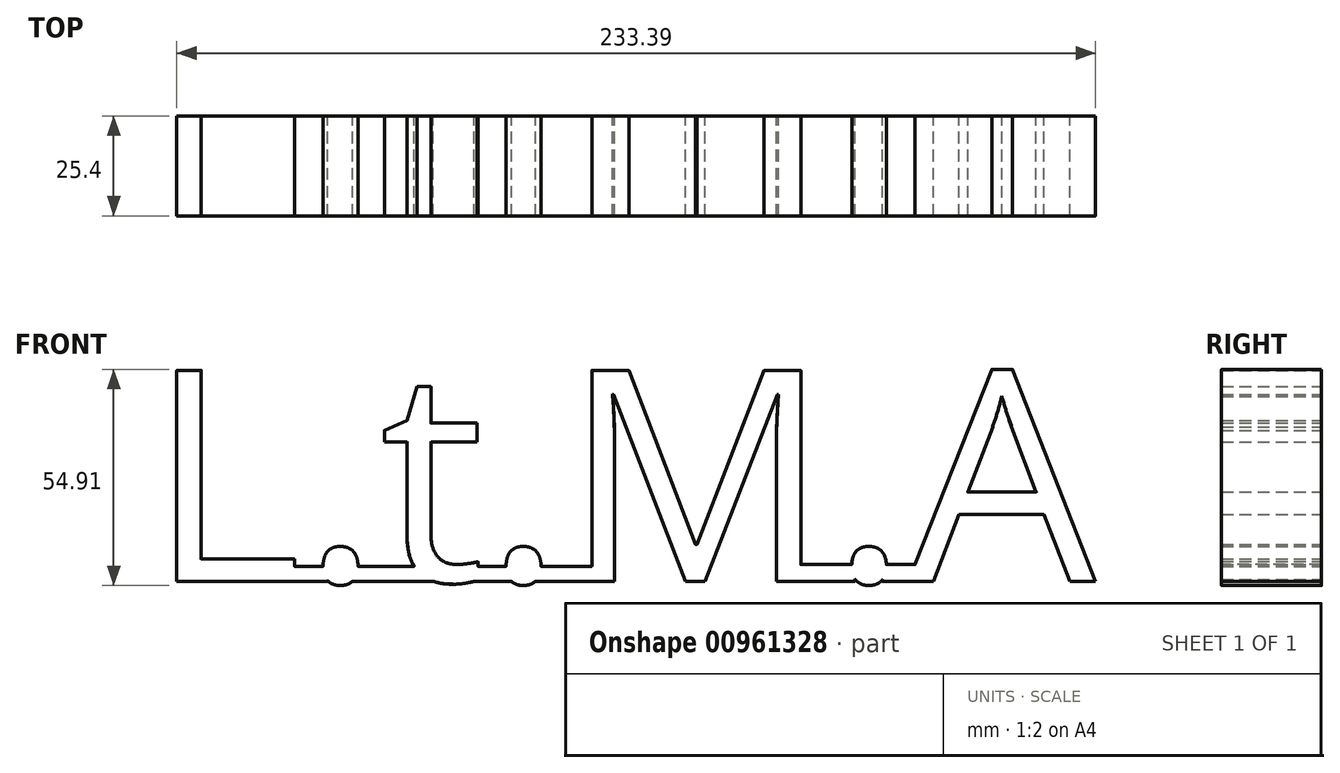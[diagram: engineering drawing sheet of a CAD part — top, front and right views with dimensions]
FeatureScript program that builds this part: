
annotation { "Feature Type Name" : "Feature", "Feature Type Description" : "" }
export const myFeature = defineFeature(function(context is Context, id is Id, definition is map)
    precondition{}
    {
        {
            var Q0;
            Q0=qCreatedBy(makeId("Front.planeOp"),FACE);
            var sketch = newSketch(context, id + "F0", { "sketchPlane" : qUnion([Q0])});
            skText(sketch, "E0", { "text": "L.t.M.A\n", "fontName": "OpenSans-Regular.ttf"});
            skLineSegment(sketch, "E1.bottom", {"start": v(-117.54, 3.84) * mm, "end": v(-107.1, 3.84) * mm});
            skLineSegment(sketch, "E1.top", {"start": v(-117.54, 0) * mm, "end": v(-107.1, 0) * mm});
            skLineSegment(sketch, "E1.left", {"start": v(-117.54, 3.84) * mm, "end": v(-117.54, 0) * mm});
            skLineSegment(sketch, "E1.right", {"start": v(-107.1, 3.84) * mm, "end": v(-107.1, 0) * mm});
            skLineSegment(sketch, "E2.bottom", {"start": v(-103.19, 3.84) * mm, "end": v(-79.7, 3.84) * mm});
            skLineSegment(sketch, "E2.top", {"start": v(-103.19, 0) * mm, "end": v(-79.7, 0) * mm});
            skLineSegment(sketch, "E2.left", {"start": v(-103.19, 3.84) * mm, "end": v(-103.19, 0) * mm});
            skLineSegment(sketch, "E2.right", {"start": v(-79.7, 3.84) * mm, "end": v(-79.7, 0) * mm});
            skLineSegment(sketch, "E3.bottom", {"start": v(-72.74, 3.84) * mm, "end": v(-59.3, 3.84) * mm});
            skLineSegment(sketch, "E3.top", {"start": v(-72.74, 0) * mm, "end": v(-59.3, 0) * mm});
            skLineSegment(sketch, "E3.left", {"start": v(-72.74, 3.84) * mm, "end": v(-72.74, 0) * mm});
            skLineSegment(sketch, "E3.right", {"start": v(-59.3, 3.84) * mm, "end": v(-59.3, 0) * mm});
            skLineSegment(sketch, "E4.bottom", {"start": v(-55.34, 3.84) * mm, "end": v(-39.66, 3.84) * mm});
            skLineSegment(sketch, "E4.top", {"start": v(-55.34, 0) * mm, "end": v(-39.66, 0) * mm});
            skLineSegment(sketch, "E4.left", {"start": v(-55.34, 3.84) * mm, "end": v(-55.34, 0) * mm});
            skLineSegment(sketch, "E4.right", {"start": v(-39.66, 3.84) * mm, "end": v(-39.66, 0) * mm});
            skLineSegment(sketch, "E5.bottom", {"start": v(9.47, 4.28) * mm, "end": v(26.87, 4.28) * mm});
            skLineSegment(sketch, "E5.top", {"start": v(9.47, 0) * mm, "end": v(26.87, 0) * mm});
            skLineSegment(sketch, "E5.left", {"start": v(9.47, 4.28) * mm, "end": v(9.47, 0) * mm});
            skLineSegment(sketch, "E5.right", {"start": v(26.87, 4.28) * mm, "end": v(26.87, 0) * mm});
            skLineSegment(sketch, "E6.bottom", {"start": v(33.83, 4.28) * mm, "end": v(42.77, 4.28) * mm});
            skLineSegment(sketch, "E6.top", {"start": v(33.83, 0) * mm, "end": v(42.77, 0) * mm});
            skLineSegment(sketch, "E6.left", {"start": v(33.83, 4.28) * mm, "end": v(33.83, 0) * mm});
            skLineSegment(sketch, "E6.right", {"start": v(42.77, 4.28) * mm, "end": v(42.77, 0) * mm});
            skLineSegment(sketch, "E7.bottom", {"start": v(-146.32, 54.07) * mm, "end": v(-138.54, 54.07) * mm});
            skLineSegment(sketch, "E7.top", {"start": v(-146.32, 95.77) * mm, "end": v(-138.54, 95.77) * mm});
            skLineSegment(sketch, "E7.left", {"start": v(-146.32, 54.07) * mm, "end": v(-146.32, 95.77) * mm});
            skLineSegment(sketch, "E7.right", {"start": v(-138.54, 54.07) * mm, "end": v(-138.54, 95.77) * mm});
            const initialGuessF0  = {"E0": [-0.1528, 0, 1, 0, 0.05407]};
            skSetInitialGuess(sketch, initialGuessF0);
            skSolve(sketch);
        }
        {
            var Q0;
            Q0 = qSketchRegion(id + "F0", true);
            extrude(context, id + "F1", {"entities" : qUnion([Q0]), "depth" : 25.4 * mm, "offsetDistance" : 25.4 * mm});
        }
        {
            var Q0;
            Q0=makeQuery(id+"F1.opExtrude","CAP_EDGE",EDGE,{"disambiguationData":[OSD([sQuery(id+"F0.wireOp",EDGE,"E0.sketch_text.stroke-0")])],"isStart":false});
            var Q1;
            Q1=makeQuery(id+"F1.opExtrude","CAP_EDGE",EDGE,{"disambiguationData":[OSD([sQuery(id+"F0.wireOp",EDGE,"E0.sketch_text.stroke-3")])],"isStart":false});
            var Q2;
            Q2=makeQuery(id+"F1.opExtrude","CAP_EDGE",EDGE,{"disambiguationData":[OSD([sQuery(id+"F0.wireOp",EDGE,"E0.sketch_text.stroke-5"),sQuery(id+"F0.wireOp",EDGE,"E1.top")])],"isStart":false});
            var Q3;
            Q3=makeQuery(id+"F1.opExtrude","CAP_FACE",FACE,{"disambiguationData":[OSD([sQuery(id+"F0.wireOp",EDGE,"E0.sketch_text.stroke-0"),sQuery(id+"F0.wireOp",EDGE,"E0.sketch_text.stroke-1"),sQuery(id+"F0.wireOp",EDGE,"E0.sketch_text.stroke-2"),sQuery(id+"F0.wireOp",EDGE,"E0.sketch_text.stroke-3"),sQuery(id+"F0.wireOp",EDGE,"E0.sketch_text.stroke-4"),sQuery(id+"F0.wireOp",EDGE,"E0.sketch_text.stroke-5"),sQuery(id+"F0.wireOp",EDGE,"E0.sketch_text.stroke-6"),sQuery(id+"F0.wireOp",EDGE,"E0.sketch_text.stroke-7"),sQuery(id+"F0.wireOp",EDGE,"E0.sketch_text.stroke-8"),sQuery(id+"F0.wireOp",EDGE,"E0.sketch_text.stroke-9"),sQuery(id+"F0.wireOp",EDGE,"E0.sketch_text.stroke-10"),sQuery(id+"F0.wireOp",EDGE,"E0.sketch_text.stroke-11"),sQuery(id+"F0.wireOp",EDGE,"E0.sketch_text.stroke-12"),sQuery(id+"F0.wireOp",EDGE,"E0.sketch_text.stroke-13"),sQuery(id+"F0.wireOp",EDGE,"E0.sketch_text.stroke-14"),sQuery(id+"F0.wireOp",EDGE,"E0.sketch_text.stroke-15"),sQuery(id+"F0.wireOp",EDGE,"E0.sketch_text.stroke-16"),sQuery(id+"F0.wireOp",EDGE,"E0.sketch_text.stroke-17"),sQuery(id+"F0.wireOp",EDGE,"E0.sketch_text.stroke-18"),sQuery(id+"F0.wireOp",EDGE,"E0.sketch_text.stroke-19"),sQuery(id+"F0.wireOp",EDGE,"E0.sketch_text.stroke-20"),sQuery(id+"F0.wireOp",EDGE,"E0.sketch_text.stroke-21"),sQuery(id+"F0.wireOp",EDGE,"E0.sketch_text.stroke-22"),sQuery(id+"F0.wireOp",EDGE,"E0.sketch_text.stroke-23"),sQuery(id+"F0.wireOp",EDGE,"E0.sketch_text.stroke-24"),sQuery(id+"F0.wireOp",EDGE,"E0.sketch_text.stroke-25"),sQuery(id+"F0.wireOp",EDGE,"E0.sketch_text.stroke-26"),sQuery(id+"F0.wireOp",EDGE,"E0.sketch_text.stroke-27"),sQuery(id+"F0.wireOp",EDGE,"E0.sketch_text.stroke-28"),sQuery(id+"F0.wireOp",EDGE,"E0.sketch_text.stroke-29"),sQuery(id+"F0.wireOp",EDGE,"E0.sketch_text.stroke-30"),sQuery(id+"F0.wireOp",EDGE,"E0.sketch_text.stroke-31"),sQuery(id+"F0.wireOp",EDGE,"E0.sketch_text.stroke-32"),sQuery(id+"F0.wireOp",EDGE,"E0.sketch_text.stroke-33"),sQuery(id+"F0.wireOp",EDGE,"E0.sketch_text.stroke-34"),sQuery(id+"F0.wireOp",EDGE,"E0.sketch_text.stroke-35"),sQuery(id+"F0.wireOp",EDGE,"E0.sketch_text.stroke-36"),sQuery(id+"F0.wireOp",EDGE,"E0.sketch_text.stroke-37"),sQuery(id+"F0.wireOp",EDGE,"E0.sketch_text.stroke-38"),sQuery(id+"F0.wireOp",EDGE,"E0.sketch_text.stroke-39"),sQuery(id+"F0.wireOp",EDGE,"E0.sketch_text.stroke-40"),sQuery(id+"F0.wireOp",EDGE,"E0.sketch_text.stroke-41"),sQuery(id+"F0.wireOp",EDGE,"E0.sketch_text.stroke-42"),sQuery(id+"F0.wireOp",EDGE,"E0.sketch_text.stroke-43"),sQuery(id+"F0.wireOp",EDGE,"E0.sketch_text.stroke-44"),sQuery(id+"F0.wireOp",EDGE,"E0.sketch_text.stroke-45"),sQuery(id+"F0.wireOp",EDGE,"E0.sketch_text.stroke-46"),sQuery(id+"F0.wireOp",EDGE,"E0.sketch_text.stroke-47"),sQuery(id+"F0.wireOp",EDGE,"E0.sketch_text.stroke-48"),sQuery(id+"F0.wireOp",EDGE,"E0.sketch_text.stroke-49"),sQuery(id+"F0.wireOp",EDGE,"E0.sketch_text.stroke-50"),sQuery(id+"F0.wireOp",EDGE,"E0.sketch_text.stroke-51"),sQuery(id+"F0.wireOp",EDGE,"E0.sketch_text.stroke-52"),sQuery(id+"F0.wireOp",EDGE,"E0.sketch_text.stroke-53"),sQuery(id+"F0.wireOp",EDGE,"E0.sketch_text.stroke-54"),sQuery(id+"F0.wireOp",EDGE,"E0.sketch_text.stroke-55"),sQuery(id+"F0.wireOp",EDGE,"E0.sketch_text.stroke-56"),sQuery(id+"F0.wireOp",EDGE,"E0.sketch_text.stroke-57"),sQuery(id+"F0.wireOp",EDGE,"E0.sketch_text.stroke-58"),sQuery(id+"F0.wireOp",EDGE,"E0.sketch_text.stroke-59"),sQuery(id+"F0.wireOp",EDGE,"E0.sketch_text.stroke-60"),sQuery(id+"F0.wireOp",EDGE,"E0.sketch_text.stroke-61"),sQuery(id+"F0.wireOp",EDGE,"E0.sketch_text.stroke-62"),sQuery(id+"F0.wireOp",EDGE,"E0.sketch_text.stroke-63"),sQuery(id+"F0.wireOp",EDGE,"E0.sketch_text.stroke-64"),sQuery(id+"F0.wireOp",EDGE,"E0.sketch_text.stroke-65"),sQuery(id+"F0.wireOp",EDGE,"E0.sketch_text.stroke-66"),sQuery(id+"F0.wireOp",EDGE,"E0.sketch_text.stroke-67"),sQuery(id+"F0.wireOp",EDGE,"E0.sketch_text.stroke-68"),sQuery(id+"F0.wireOp",EDGE,"E0.sketch_text.stroke-69"),sQuery(id+"F0.wireOp",EDGE,"E0.sketch_text.stroke-70"),sQuery(id+"F0.wireOp",EDGE,"E0.sketch_text.stroke-71"),sQuery(id+"F0.wireOp",EDGE,"E0.sketch_text.stroke-72"),sQuery(id+"F0.wireOp",EDGE,"E0.sketch_text.stroke-73"),sQuery(id+"F0.wireOp",EDGE,"E0.sketch_text.stroke-74"),sQuery(id+"F0.wireOp",EDGE,"E0.sketch_text.stroke-75"),sQuery(id+"F0.wireOp",EDGE,"E0.sketch_text.stroke-76"),sQuery(id+"F0.wireOp",EDGE,"E0.sketch_text.stroke-77"),sQuery(id+"F0.wireOp",EDGE,"E0.sketch_text.stroke-78"),sQuery(id+"F0.wireOp",EDGE,"E0.sketch_text.stroke-79"),sQuery(id+"F0.wireOp",EDGE,"E1.bottom"),sQuery(id+"F0.wireOp",EDGE,"E1.top"),sQuery(id+"F0.wireOp",EDGE,"E1.right"),sQuery(id+"F0.wireOp",EDGE,"E2.bottom"),sQuery(id+"F0.wireOp",EDGE,"E2.top"),sQuery(id+"F0.wireOp",EDGE,"E3.bottom"),sQuery(id+"F0.wireOp",EDGE,"E3.top"),sQuery(id+"F0.wireOp",EDGE,"E4.bottom"),sQuery(id+"F0.wireOp",EDGE,"E4.top"),sQuery(id+"F0.wireOp",EDGE,"E5.bottom"),sQuery(id+"F0.wireOp",EDGE,"E5.top"),sQuery(id+"F0.wireOp",EDGE,"E5.right"),sQuery(id+"F0.wireOp",EDGE,"E6.bottom"),sQuery(id+"F0.wireOp",EDGE,"E6.top"),sQuery(id+"F0.wireOp",EDGE,"E6.left")])],"isStart":false});
            var Q4;
            Q4=makeQuery(id+"F1.opExtrude","CAP_EDGE",EDGE,{"disambiguationData":[OSD([sQuery(id+"F0.wireOp",EDGE,"E1.bottom")])],"isStart":false});
            var Q5;
            Q5=makeQuery(id+"F1.opExtrude","CAP_EDGE",EDGE,{"disambiguationData":[OSD([sQuery(id+"F0.wireOp",EDGE,"E0.sketch_text.stroke-2")])],"isStart":false});
            fillet(context, id + "F2", {"entities" : qUnion([Q0, Q1, Q2, Q3, Q4, Q5]), "radius" : 0.02 * mm, "tangentPropagation" : true, "allowEdgeOverflow" : false});
        }
        {
            var Q0;
            Q0=makeQuery(id+"F1.opExtrude","SWEPT_BODY",BODY,{"disambiguationData":[OSD([sQuery(id+"F0.wireOp",EDGE,"E7.bottom"),sQuery(id+"F0.wireOp",EDGE,"E7.top"),sQuery(id+"F0.wireOp",EDGE,"E7.left"),sQuery(id+"F0.wireOp",EDGE,"E7.right")])]});
            deleteBodies(context, id + "F3", {"entities" : qUnion([Q0])});
        }
        {
            var Q0;
            Q0=sQuery(id+"F0.wireOp",EDGE,"E7.right");
            extrude(context, id + "F4", {"bodyType" : ToolBodyType.SURFACE, "surfaceEntities" : qUnion([Q0]), "depth" : 25 * mm, "offsetDistance" : 25 * mm});
        }
        {
            var Q0;
            Q0=makeQuery(id+"F4.opExtrude","SWEPT_BODY",BODY,{"disambiguationData":[OSD([sQuery(id+"F0.wireOp",EDGE,"E7.right")])]});
            deleteBodies(context, id + "F5", {"entities" : qUnion([Q0])});
        }
    });
